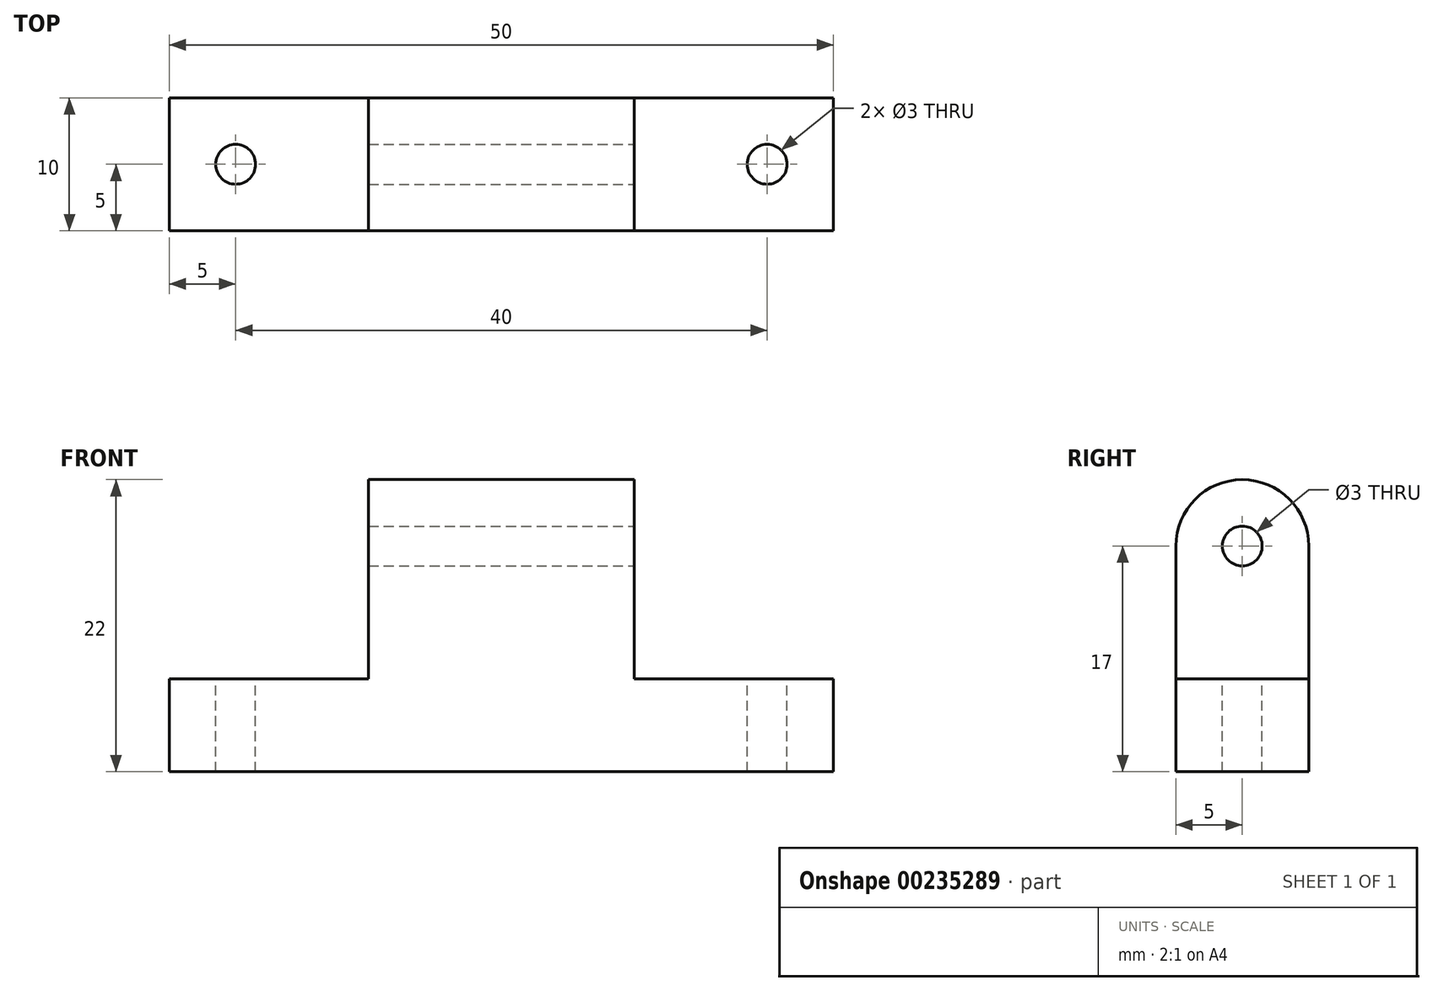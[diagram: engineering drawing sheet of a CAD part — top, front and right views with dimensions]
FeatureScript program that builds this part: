
annotation { "Feature Type Name" : "Feature", "Feature Type Description" : "" }
export const myFeature = defineFeature(function(context is Context, id is Id, definition is map)
    precondition{}
    {
        {
            var Q0;
            Q0=qCreatedBy(makeId("Top.planeOp"),FACE);
            var sketch = newSketch(context, id + "F0", { "sketchPlane" : qUnion([Q0])});
            skLineSegment(sketch, "E0.bottom", {"start": v(0, 0) * mm, "end": v(50, 0) * mm});
            skLineSegment(sketch, "E0.top", {"start": v(0, 10) * mm, "end": v(50, 10) * mm});
            skLineSegment(sketch, "E0.left", {"start": v(0, 0) * mm, "end": v(0, 10) * mm});
            skLineSegment(sketch, "E0.right", {"start": v(50, 0) * mm, "end": v(50, 10) * mm});
            skSolve(sketch);
        }
        {
            var Q0;
            Q0=qSketchRegion(id+"F0",true);
            extrude(context, id + "F1", {"entities" : qUnion([Q0]), "depth" : 7 * mm});
        }
        {
            var Q0;
            Q0=makeQuery(id+"F1.opExtrude","CAP_FACE",FACE,{"disambiguationData":[OSD([sQuery(id+"F0.wireOp",EDGE,"E0.bottom"),sQuery(id+"F0.wireOp",EDGE,"E0.top"),sQuery(id+"F0.wireOp",EDGE,"E0.left"),sQuery(id+"F0.wireOp",EDGE,"E0.right")])],"isStart":false});
            var sketch = newSketch(context, id + "F2", { "sketchPlane" : qUnion([Q0])});
            skLineSegment(sketch, "E1.bottom", {"start": v(15, 0) * mm, "end": v(35, 0) * mm});
            skLineSegment(sketch, "E1.top", {"start": v(15, 10) * mm, "end": v(35, 10) * mm});
            skLineSegment(sketch, "E1.left", {"start": v(15, 0) * mm, "end": v(15, 10) * mm});
            skLineSegment(sketch, "E1.right", {"start": v(35, 0) * mm, "end": v(35, 10) * mm});
            skSolve(sketch);
        }
        {
            var Q0;
            {var subQ0=sQuery(id+"F2.wireOp",EDGE,"E1.right");Q0=makeQuery(id+"F2.imprint","IMPRINT",FACE,{"disambiguationData":[TD([[makeQuery(id+"F2.imprint","IMPRINT",EDGE,{"derivedFrom":subQ0}),-1.0]])]});}
            var sketch = newSketch(context, id + "F3", { "sketchPlane" : qUnion([Q0])});
            skCircle(sketch, "E2", {"center": v(45, 5) * mm, "radius": 1.5 * mm});
            skCircle(sketch, "E3", {"center": v(5, 5) * mm, "radius": 1.5 * mm});
            skSolve(sketch);
        }
        {
            var Q0;
            Q0=qSketchRegion(id+"F2",true);
            extrude(context, id + "F4", {"entities" : qUnion([Q0]), "operationType" : NewBodyOperationType.ADD, "depth" : 15 * mm});
        }
        {
            var Q0;
            Q0=makeQuery(id+"F4.opExtrude","CAP_EDGE",EDGE,{"disambiguationData":[OSD([sQuery(id+"F2.wireOp",EDGE,"E1.top")])],"isStart":false});
            var Q1;
            Q1=makeQuery(id+"F4.opExtrude","CAP_EDGE",EDGE,{"disambiguationData":[OSD([sQuery(id+"F2.wireOp",EDGE,"E1.bottom")])],"isStart":false});
            fillet(context, id + "F5", {"entities" : qUnion([Q0, Q1]), "radius" : 5 * mm, "tangentPropagation" : true, "allowEdgeOverflow" : false});
        }
        {
            var Q0;
            Q0=qSketchRegion(id+"F3",true);
            extrude(context, id + "F6", {"entities" : qUnion([Q0]), "operationType" : NewBodyOperationType.REMOVE, "oppositeDirection" : true, "depth" : 25 * mm});
        }
        {
            var Q0;
            Q0=makeQuery(id+"F4.opExtrude","SWEPT_FACE",FACE,{"disambiguationData":[OSD([sQuery(id+"F2.wireOp",EDGE,"E1.right")])]});
            var sketch = newSketch(context, id + "F7", { "sketchPlane" : qUnion([Q0])});
            skCircle(sketch, "E4", {"center": v(5, 17) * mm, "radius": 1.5 * mm});
            skSolve(sketch);
        }
        {
            var Q0;
            Q0=qSketchRegion(id+"F7",true);
            extrude(context, id + "F8", {"entities" : qUnion([Q0]), "operationType" : NewBodyOperationType.REMOVE, "oppositeDirection" : true, "depth" : 50 * mm});
        }
        {
            var Q0;
            Q0=makeQuery(id+"F1.opExtrude","SWEPT_BODY",BODY,{"disambiguationData":[OSD([sQuery(id+"F0.wireOp",EDGE,"E0.bottom"),sQuery(id+"F0.wireOp",EDGE,"E0.top"),sQuery(id+"F0.wireOp",EDGE,"E0.left"),sQuery(id+"F0.wireOp",EDGE,"E0.right")])]});
            transform(context, id + "F9", {"entities" : qUnion([Q0]), "transformType" : TransformType.TRANSLATION_3D, "dx" : 0 * mm, "dy" : 0 * mm, "dz" : 40 * mm, "makeCopy" : true});
        }
        {
            var Q0;
            Q0=makeQuery(id+"F9.opPattern","COPY",FACE,{"derivedFrom":makeQuery(id+"F1.opExtrude","CAP_FACE",FACE,{"disambiguationData":[OSD([sQuery(id+"F0.wireOp",EDGE,"E0.bottom"),sQuery(id+"F0.wireOp",EDGE,"E0.top"),sQuery(id+"F0.wireOp",EDGE,"E0.left"),sQuery(id+"F0.wireOp",EDGE,"E0.right")])],"isStart":false}),"instanceName":"1"});
            var sketch = newSketch(context, id + "F10", { "sketchPlane" : qUnion([Q0])});
            skLineSegment(sketch, "E5.bottom", {"start": v(20, 10) * mm, "end": v(30, 10) * mm});
            skLineSegment(sketch, "E5.top", {"start": v(20, 0) * mm, "end": v(30, 0) * mm});
            skLineSegment(sketch, "E5.left", {"start": v(20, 10) * mm, "end": v(20, 0) * mm});
            skLineSegment(sketch, "E5.right", {"start": v(30, 10) * mm, "end": v(30, 0) * mm});
            skSolve(sketch);
        }
        {
            var Q0;
            Q0=qSketchRegion(id+"F10",true);
            extrude(context, id + "F11", {"entities" : qUnion([Q0]), "operationType" : NewBodyOperationType.REMOVE, "depth" : 25 * mm});
        }
        {
            var Q0;
            Q0=makeQuery(id+"F9.opPattern","COPY",BODY,{"derivedFrom":makeQuery(id+"F1.opExtrude","SWEPT_BODY",BODY,{"disambiguationData":[OSD([sQuery(id+"F0.wireOp",EDGE,"E0.bottom"),sQuery(id+"F0.wireOp",EDGE,"E0.top"),sQuery(id+"F0.wireOp",EDGE,"E0.left"),sQuery(id+"F0.wireOp",EDGE,"E0.right")])]}),"instanceName":"1"});
            deleteBodies(context, id + "F12", {"entities" : qUnion([Q0])});
        }
    });
